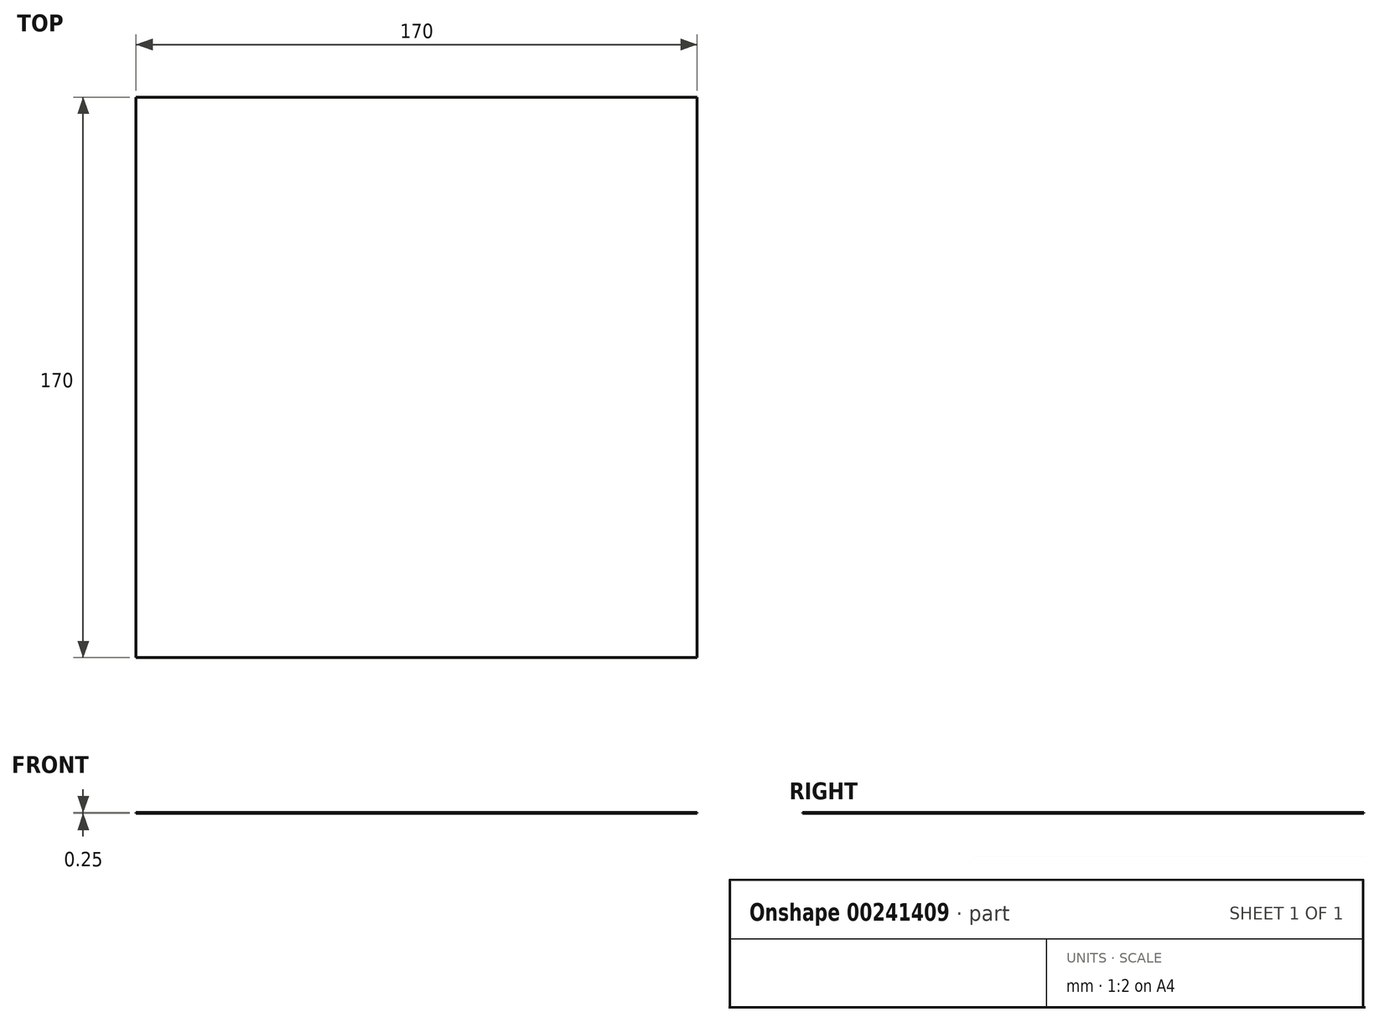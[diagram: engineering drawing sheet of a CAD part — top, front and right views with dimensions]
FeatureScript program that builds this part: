
annotation { "Feature Type Name" : "Feature", "Feature Type Description" : "" }
export const myFeature = defineFeature(function(context is Context, id is Id, definition is map)
    precondition{}
    {
        {
            var Q0;
            Q0=qCreatedBy(makeId("Top.planeOp"),FACE);
            var sketch = newSketch(context, id + "F0", { "sketchPlane" : qUnion([Q0])});
            skLineSegment(sketch, "E0.bottom", {"start": v(-85, 85) * mm, "end": v(85, 85) * mm});
            skLineSegment(sketch, "E0.top", {"start": v(-85, -85) * mm, "end": v(85, -85) * mm});
            skLineSegment(sketch, "E0.left", {"start": v(-85, 85) * mm, "end": v(-85, -85) * mm});
            skLineSegment(sketch, "E0.right", {"start": v(85, 85) * mm, "end": v(85, -85) * mm});
            skPoint(sketch, "E0.middle", {"position": v(0, 0) * mm});
            skSolve(sketch);
        }
        {
            var Q0;
            Q0 = qSketchRegion(id + "F0", true);
            extrude(context, id + "F1", {"entities" : qUnion([Q0]), "depth" : .25 * mm});
        }
    });
